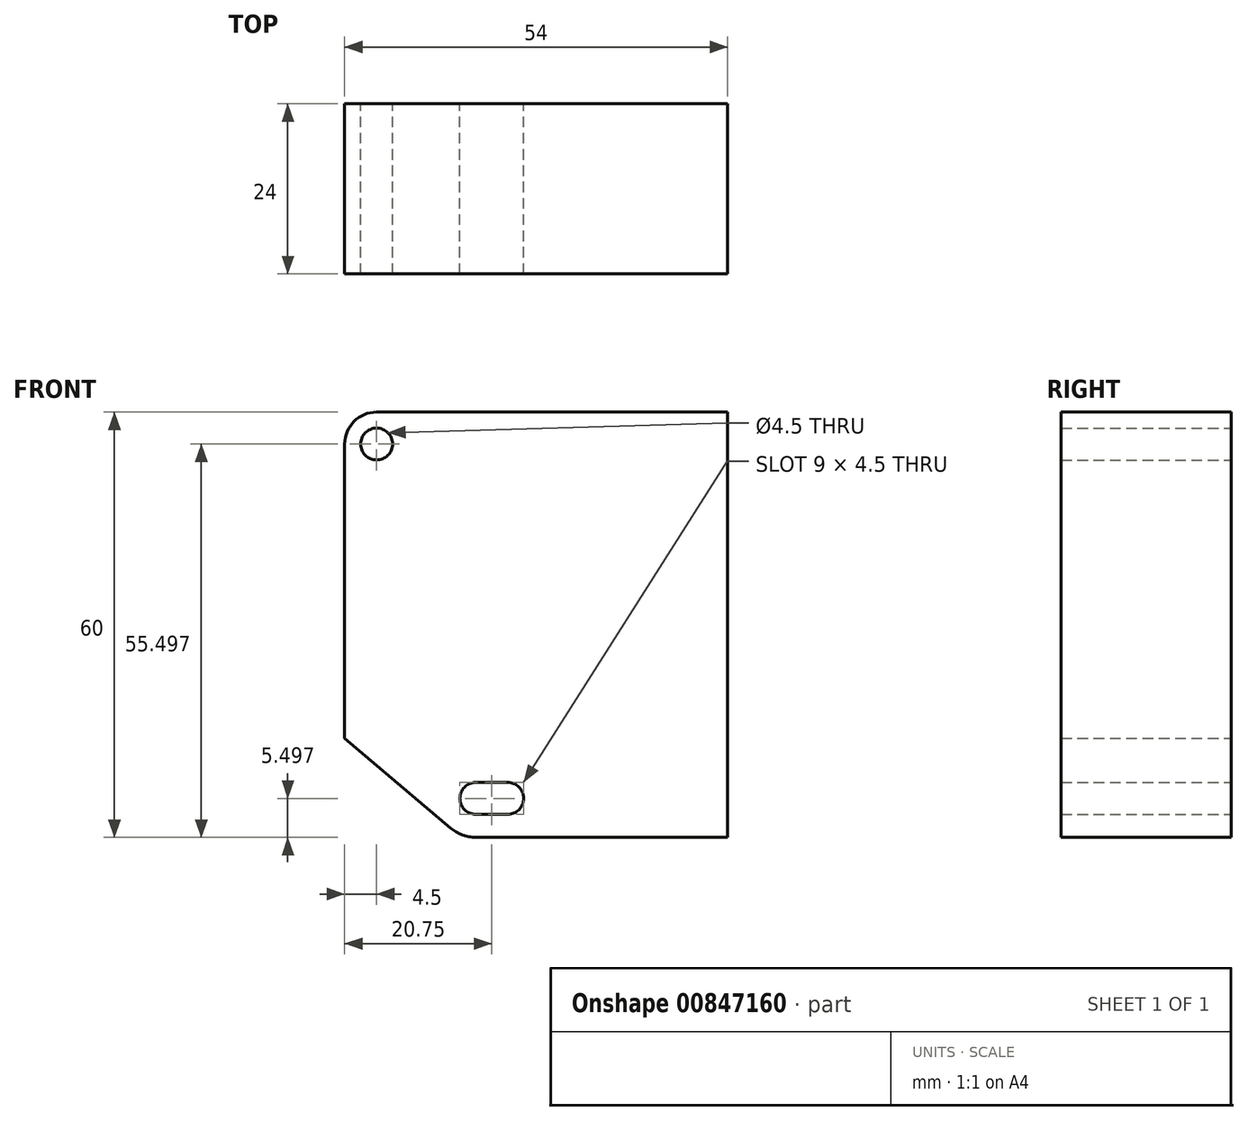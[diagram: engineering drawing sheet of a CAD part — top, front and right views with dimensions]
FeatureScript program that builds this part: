
annotation { "Feature Type Name" : "Feature", "Feature Type Description" : "" }
export const myFeature = defineFeature(function(context is Context, id is Id, definition is map)
    precondition{}
    {
        {
            var Q0;
            Q0=qCreatedBy(makeId("Front.planeOp"),FACE);
            var sketch = newSketch(context, id + "F0", { "sketchPlane" : qUnion([Q0])});
            skLineSegment(sketch, "E0", {"start": v(-15.94, 35.23) * mm, "end": v(33.56, 35.23) * mm});
            skLineSegment(sketch, "E1", {"start": v(33.56, 35.23) * mm, "end": v(33.56, -24.77) * mm});
            skLineSegment(sketch, "E2", {"start": v(33.56, -24.77) * mm, "end": v(-3.96, -24.77) * mm});
            skLineSegment(sketch, "E3", {"start": v(-20.44, -10.77) * mm, "end": v(-20.44, 30.73) * mm});
            skLineSegment(sketch, "E4", {"start": v(-20.44, -10.77) * mm, "end": v(-6.44, -10.77) * mm, "construction": true});
            skLineSegment(sketch, "E5", {"start": v(-6.44, -10.77) * mm, "end": v(-6.44, -24.77) * mm, "construction": true});
            skLineSegment(sketch, "E6", {"start": v(33.56, -24.77) * mm, "end": v(33.56, -37.77) * mm, "construction": true});
            skPoint(sketch, "E7.visualSharp", {"position": v(-20.44, 35.23) * mm});
            skArc(sketch, "E7.filletArc", {"start": v(-15.94, 35.23) * mm, "mid": v(-19.12, 33.9) * mm, "end": v(-20.44, 30.73) * mm});
            skCircle(sketch, "E8", {"center": v(-15.94, 30.73) * mm, "radius": 2.25 * mm});
            skLineSegment(sketch, "E9", {"start": v(-15.94, 30.73) * mm, "end": v(-1.94, 30.73) * mm, "construction": true});
            skLineSegment(sketch, "E10", {"start": v(-1.94, 30.73) * mm, "end": v(-1.94, -24.77) * mm, "construction": true});
            skLineSegment(sketch, "E11", {"start": v(-15.94, 30.73) * mm, "end": v(-15.94, -19.27) * mm, "construction": true});
            skLineSegment(sketch, "E12", {"start": v(-15.94, -19.27) * mm, "end": v(71.27, -19.27) * mm, "construction": true});
            skArc(sketch, "E13", {"start": v(-1.94, -17.02) * mm, "mid": v(-4.19, -19.27) * mm, "end": v(-1.94, -21.52) * mm});
            skArc(sketch, "E14", {"start": v(-1.94, -13.77) * mm, "mid": v(-7.44, -19.27) * mm, "end": v(-1.94, -24.77) * mm});
            skLineSegment(sketch, "E15", {"start": v(0.31, -19.27) * mm, "end": v(0.31, -17.02) * mm, "construction": true});
            skArc(sketch, "E16.MirrorC", {"start": v(2.56, -17.02) * mm, "mid": v(4.81, -19.27) * mm, "end": v(2.56, -21.52) * mm});
            skLineSegment(sketch, "E17", {"start": v(-1.94, -13.77) * mm, "end": v(2.56, -13.77) * mm});
            skLineSegment(sketch, "E18", {"start": v(-1.94, -17.02) * mm, "end": v(2.56, -17.02) * mm});
            skLineSegment(sketch, "E19", {"start": v(-1.94, -21.52) * mm, "end": v(2.56, -21.52) * mm});
            skArc(sketch, "E20.trimOffspring", {"start": v(2.56, -24.77) * mm, "mid": v(8.06, -19.27) * mm, "end": v(2.56, -13.77) * mm});
            skLineSegment(sketch, "E21", {"start": v(-20.44, -10.77) * mm, "end": v(-3.96, -24.77) * mm});
            skLineSegment(sketch, "E22", {"start": v(-18.19, -58.25) * mm, "end": v(-10.25, -58.25) * mm, "construction": true});
            skLineSegment(sketch, "E23", {"start": v(-10.25, -58.25) * mm, "end": v(-6.44, -22.67) * mm, "construction": true});
            skLineSegment(sketch, "E24", {"start": v(-18.19, -12.68) * mm, "end": v(-18.19, -32.68) * mm});
            skLineSegment(sketch, "E25", {"start": v(-18.19, -32.68) * mm, "end": v(-10.19, -32.68) * mm});
            skLineSegment(sketch, "E26.top", {"start": v(-18.19, -37.68) * mm, "end": v(-10.19, -37.68) * mm});
            skLineSegment(sketch, "E26.left", {"start": v(-18.19, -32.68) * mm, "end": v(-18.19, -37.68) * mm});
            skLineSegment(sketch, "E26.right", {"start": v(-10.19, -32.68) * mm, "end": v(-10.19, -37.68) * mm});
            skLineSegment(sketch, "E27", {"start": v(-10.19, -32.68) * mm, "end": v(-6.44, -22.67) * mm});
            skSolve(sketch);
        }
        {
            var Q0;
            Q0=makeQuery(id+"F0.imprint","IMPRINT",FACE,{"disambiguationData":[TD([[makeQuery(id+"F0.imprint","IMPRINT",EDGE,{"derivedFrom":sQuery(id+"F0.wireOp",EDGE,"E0")}),-1.0]])]});
            var Q1;
            Q1=makeQuery(id+"F0.imprint","IMPRINT",FACE,{"disambiguationData":[TD([[makeQuery(id+"F0.imprint","IMPRINT",EDGE,{"derivedFrom":sQuery(id+"F0.wireOp",EDGE,"E13")}),-1.0]])]});
            extrude(context, id + "F1", {"entities" : qUnion([Q0, Q1]), "depth" : 24 * mm, "offsetDistance" : 25 * mm});
        }
    });
